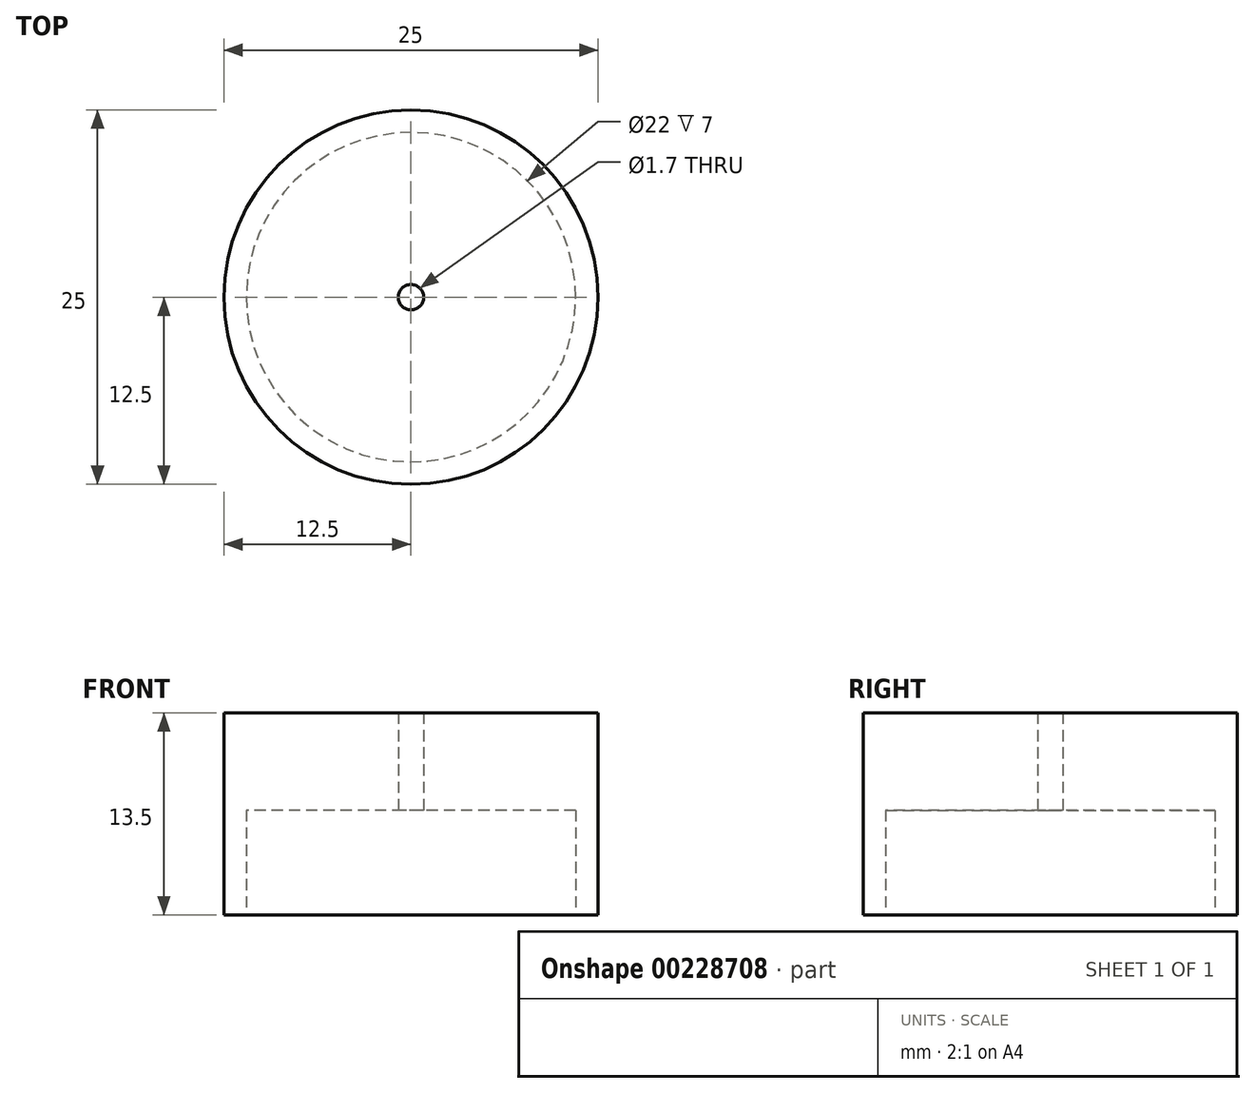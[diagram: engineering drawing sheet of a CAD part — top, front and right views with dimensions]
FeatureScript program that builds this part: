
annotation { "Feature Type Name" : "Feature", "Feature Type Description" : "" }
export const myFeature = defineFeature(function(context is Context, id is Id, definition is map)
    precondition{}
    {
        {
            var Q0;
            Q0=qCreatedBy(makeId("Top.planeOp"),FACE);
            var sketch = newSketch(context, id + "F0", { "sketchPlane" : qUnion([Q0])});
            skCircle(sketch, "E0", {"center": v(0, 0) * mm, "radius": 12.5 * mm});
            skCircle(sketch, "E1", {"center": v(0, 0) * mm, "radius": 11 * mm});
            skCircle(sketch, "E2", {"center": v(0, 0) * mm, "radius": 0.85 * mm});
            skSolve(sketch);
        }
        {
            var Q0;
            Q0=makeQuery(id+"F0.imprint","IMPRINT",FACE,{"disambiguationData":[TD([[makeQuery(id+"F0.imprint","IMPRINT",EDGE,{"derivedFrom":sQuery(id+"F0.wireOp",EDGE,"E0")}),1.0]])]});
            extrude(context, id + "F1", {"entities" : qUnion([Q0]), "depth" : 13.5 * mm});
        }
        {
            var Q0;
            Q0=makeQuery(id+"F0.imprint","IMPRINT",FACE,{"disambiguationData":[TD([[makeQuery(id+"F0.imprint","IMPRINT",EDGE,{"derivedFrom":sQuery(id+"F0.wireOp",EDGE,"E1")}),1.0]])]});
            extrude(context, id + "F2", {"entities" : qUnion([Q0]), "operationType" : NewBodyOperationType.ADD, "depth" : 13.5 * mm, "hasSecondDirection" : true, "secondDirectionOppositeDirection" : false, "secondDirectionDepth" : 7 * mm});
        }
    });
